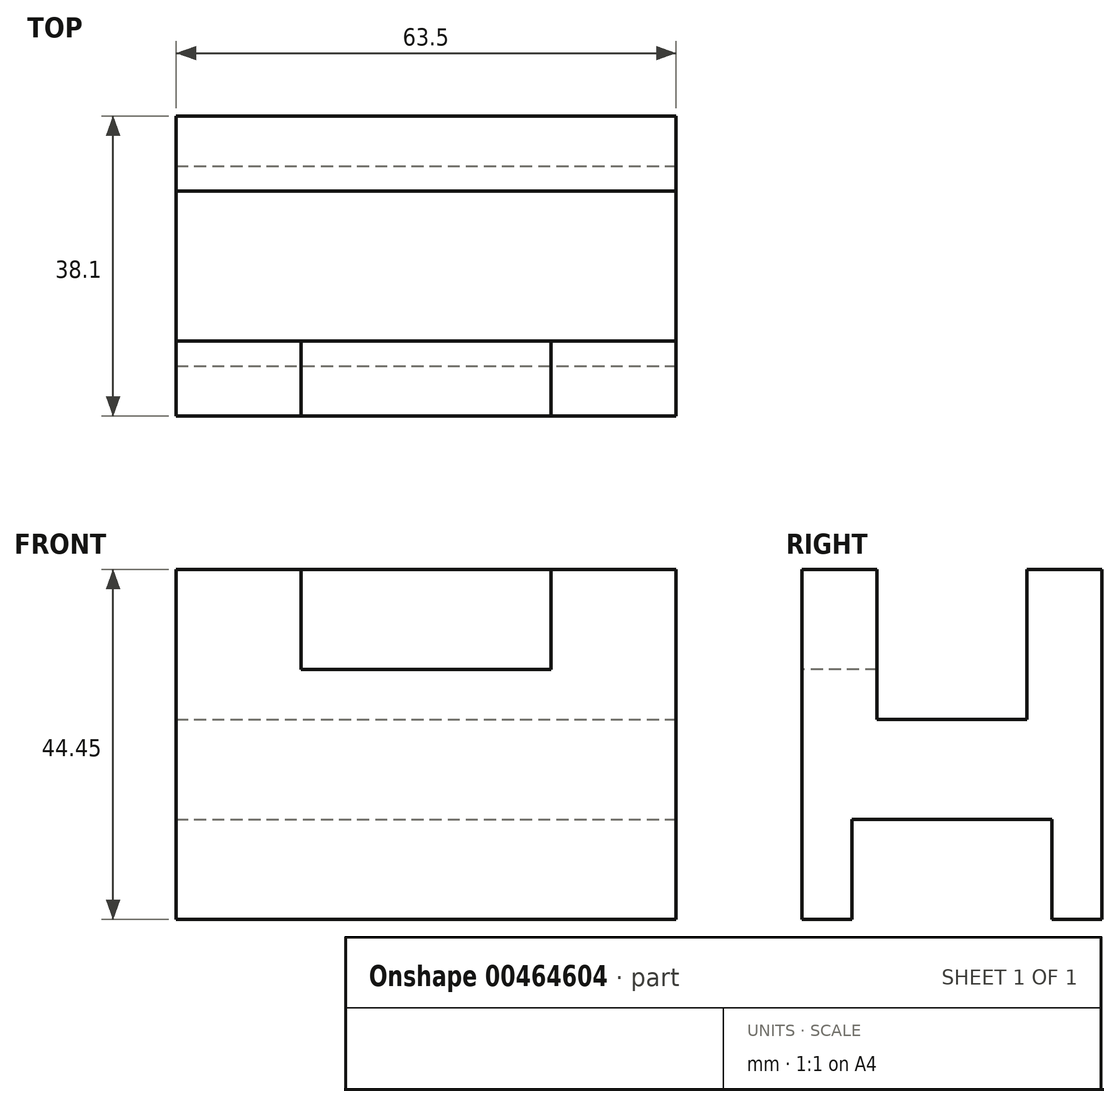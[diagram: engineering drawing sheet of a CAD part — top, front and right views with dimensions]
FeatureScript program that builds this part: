
annotation { "Feature Type Name" : "Feature", "Feature Type Description" : "" }
export const myFeature = defineFeature(function(context is Context, id is Id, definition is map)
    precondition{}
    {
        {
            var Q0;
            Q0=qCreatedBy(makeId("Front.planeOp"),FACE);
            var sketch = newSketch(context, id + "F0", { "sketchPlane" : qUnion([Q0])});
            skLineSegment(sketch, "E0.bottom", {"start": v(32.84, 26.26) * mm, "end": v(-30.66, 26.26) * mm});
            skLineSegment(sketch, "E0.top", {"start": v(32.84, -18.2) * mm, "end": v(-30.66, -18.2) * mm});
            skLineSegment(sketch, "E0.left", {"start": v(32.84, 26.26) * mm, "end": v(32.84, -18.2) * mm});
            skLineSegment(sketch, "E0.right", {"start": v(-30.66, 26.26) * mm, "end": v(-30.66, -18.2) * mm});
            skPoint(sketch, "E0.middle", {"position": v(1.1, 4.03) * mm});
            skSolve(sketch);
        }
        {
            var Q0;
            Q0=makeQuery(id+"F0.imprint","IMPRINT",FACE,{"disambiguationData":[TD([[makeQuery(id+"F0.imprint","IMPRINT",EDGE,{"derivedFrom":sQuery(id+"F0.wireOp",EDGE,"E0.bottom")}),1.0]])]});
            extrude(context, id + "F1", {"entities" : qUnion([Q0]), "depth" : 38.1 * mm});
        }
        {
            var Q0;
            Q0=makeQuery(id+"F1.opExtrude","SWEPT_FACE",FACE,{"disambiguationData":[OSD([sQuery(id+"F0.wireOp",EDGE,"E0.left")])]});
            var sketch = newSketch(context, id + "F2", { "sketchPlane" : qUnion([Q0])});
            skLineSegment(sketch, "E1.bottom", {"start": v(-28.57, 26.26) * mm, "end": v(-9.52, 26.26) * mm});
            skLineSegment(sketch, "E1.top", {"start": v(-28.57, 7.2) * mm, "end": v(-9.53, 7.2) * mm});
            skLineSegment(sketch, "E1.left", {"start": v(-28.57, 26.26) * mm, "end": v(-28.57, 7.2) * mm});
            skLineSegment(sketch, "E1.right", {"start": v(-9.53, 26.26) * mm, "end": v(-9.53, 7.2) * mm});
            skLineSegment(sketch, "E2.bottom", {"start": v(-31.75, -18.2) * mm, "end": v(-6.35, -18.2) * mm});
            skLineSegment(sketch, "E2.top", {"start": v(-31.75, -5.5) * mm, "end": v(-6.35, -5.5) * mm});
            skLineSegment(sketch, "E2.left", {"start": v(-31.75, -18.2) * mm, "end": v(-31.75, -5.5) * mm});
            skLineSegment(sketch, "E2.right", {"start": v(-6.35, -18.2) * mm, "end": v(-6.35, -5.5) * mm});
            skSolve(sketch);
        }
        {
            var Q0;
            Q0 = qSketchRegion(id + "F2", true);
            extrude(context, id + "F3", {"entities" : qUnion([Q0]), "operationType" : NewBodyOperationType.REMOVE, "oppositeDirection" : true, "depth" : 117.86 * mm});
        }
        {
            var Q0;
            Q0=makeQuery(id+"F1.opExtrude","CAP_FACE",FACE,{"disambiguationData":[OSD([sQuery(id+"F0.wireOp",EDGE,"E0.bottom"),sQuery(id+"F0.wireOp",EDGE,"E0.top"),sQuery(id+"F0.wireOp",EDGE,"E0.left"),sQuery(id+"F0.wireOp",EDGE,"E0.right")])],"isStart":false});
            var sketch = newSketch(context, id + "F4", { "sketchPlane" : qUnion([Q0])});
            skLineSegment(sketch, "E3.bottom", {"start": v(-14.78, 26.26) * mm, "end": v(16.97, 26.26) * mm});
            skLineSegment(sketch, "E3.top", {"start": v(-14.78, 13.56) * mm, "end": v(16.97, 13.56) * mm});
            skLineSegment(sketch, "E3.left", {"start": v(-14.78, 26.26) * mm, "end": v(-14.78, 13.56) * mm});
            skLineSegment(sketch, "E3.right", {"start": v(16.97, 26.26) * mm, "end": v(16.97, 13.56) * mm});
            skSolve(sketch);
        }
        {
            var Q0;
            Q0=makeQuery(id+"F4.imprint","IMPRINT",FACE,{"disambiguationData":[TD([[makeQuery(id+"F4.imprint","IMPRINT",EDGE,{"derivedFrom":sQuery(id+"F4.wireOp",EDGE,"E3.bottom")}),1.0]])]});
            extrude(context, id + "F5", {"entities" : qUnion([Q0]), "operationType" : NewBodyOperationType.REMOVE, "oppositeDirection" : true, "depth" : 25.4 * mm});
        }
    });
